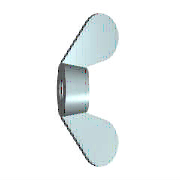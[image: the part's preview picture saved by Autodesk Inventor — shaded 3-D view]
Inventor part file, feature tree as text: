
AUTODESK INVENTOR PART (.ipt)
format: ipt  version: 2020 (Build 240168000, 168)  size: 173,568 bytes
history: native  units: mm (DEFAULTED — no unit token found)
features: sketch x2, extrude x1, mirror x1, hole x1, other x1, plane x1
ambient origin geometry x7: Origin, YZ Plane, XZ Plane, X Axis, Y Axis, Z Axis, Center Point
bodies: Solid1 (feature_tree), Body (feature_tree)
feature tree (7):
  sketch  "Sketch1"  dims[d0=10.414mm d1=9.4615mm]
  extrude  "Wing1"  Depth=9.4615mm
  mirror  "Wing2"
  hole  "Thread"  [1 undecoded]
  other  "Work Axis1"
  plane  "Work Plane1"
  sketch  "Sketch2"  dims[d2=9.9695mm d3=4.7625mm d57=90.0deg d4=8.636mm d5=11.938mm d6=4.318mm d7=0.0mm d8=1.439333mm d97=4.9784mm d98=6.0mm d99=4.0mm d100=2.0mm d101=14.3117mm d102=8.0mm d103=20.594885mm d9=0.687408mm d10=30.0deg d11=0.0mm d108=0.0mm d109=0.687408mm d110=0.0mm d111=0.0mm d112=0.0mm]
note: 1 required parameter value undecoded (feature->parameter linkage not recoverable at this tier; creation-order binding heuristic only, values carry confidence <= 0.55)
